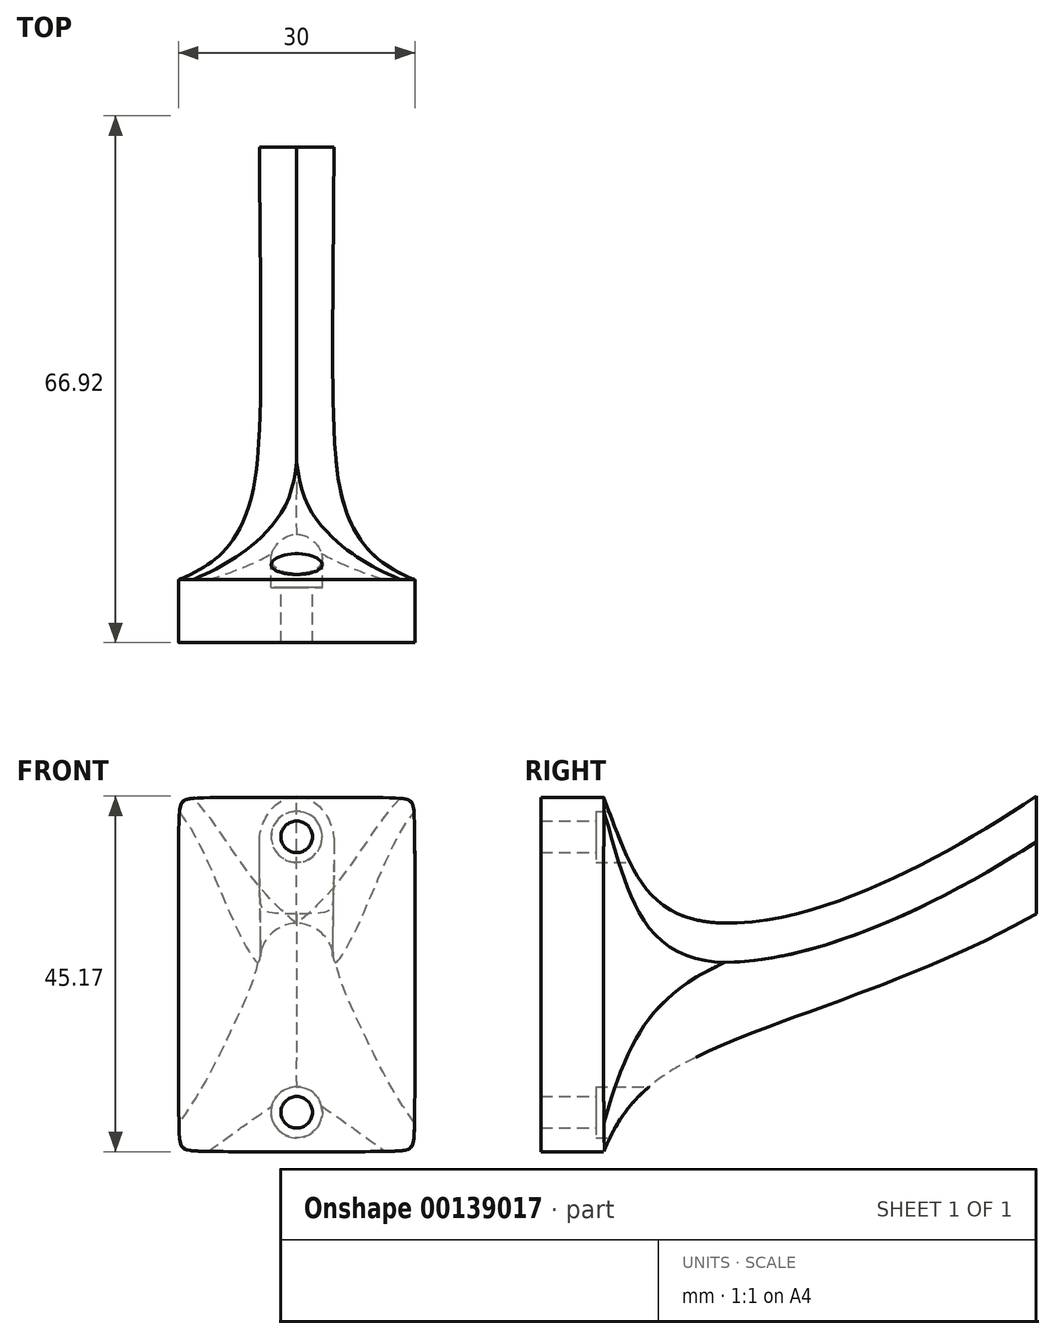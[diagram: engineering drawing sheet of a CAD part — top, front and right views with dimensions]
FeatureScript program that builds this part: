
annotation { "Feature Type Name" : "Feature", "Feature Type Description" : "" }
export const myFeature = defineFeature(function(context is Context, id is Id, definition is map)
    precondition{}
    {
        {
            var Q0;
            Q0=qCreatedBy(makeId("Right.planeOp"),FACE);
            var sketch = newSketch(context, id + "F0", { "sketchPlane" : qUnion([Q0])});
            skLineSegment(sketch, "E0", {"start": v(0, 0) * mm, "end": v(0, 45) * mm});
            skLineSegment(sketch, "E1", {"start": v(54.94, 45.17) * mm, "end": v(54.94, 30.17) * mm});
            skFitSpline(sketch, "E2", {"points": [v(0, 45) * mm, v(8.8, 30.52) * mm, v(54.94, 45.17) * mm], "startDerivative": vector(18.6, -48.26) * mm, "endDerivative": vector(97.53, 66.1) * mm});
            skFitSpline(sketch, "E3", {"points": [v(0, 0) * mm, v(8.62, 10.3) * mm, v(54.94, 30.17) * mm], "startDerivative": vector(13.75, 34.06) * mm, "endDerivative": vector(78.66, 44.42) * mm});
            skSolve(sketch);
        }
        {
            var Q0;
            Q0 = qSketchRegion(id + "F0", true);
            extrude(context, id + "F1", {"entities" : qUnion([Q0]), "endBound" : BoundingType.SYMMETRIC, "depth" : 30 * mm});
        }
        {
            var Q0;
            Q0=makeQuery(id+"F1.opExtrude","SWEPT_FACE",FACE,{"disambiguationData":[OSD([sQuery(id+"F0.wireOp",EDGE,"E0")])]});
            extrude(context, id + "F2", {"entities" : qUnion([Q0]), "operationType" : NewBodyOperationType.ADD, "depth" : 8 * mm});
        }
        {
            var Q0;
            Q0=qCreatedBy(makeId("Top.planeOp"),FACE);
            var sketch = newSketch(context, id + "F3", { "sketchPlane" : qUnion([Q0])});
            skLineSegment(sketch, "E4", {"start": v(-28.38, 62.27) * mm, "end": v(-28.38, 0) * mm});
            skLineSegment(sketch, "E5", {"start": v(-28.38, 0) * mm, "end": v(-15, 0) * mm});
            skLineSegment(sketch, "E6", {"start": v(-28.38, 62.27) * mm, "end": v(-13.4, 62.27) * mm});
            skFitSpline(sketch, "E7", {"points": [v(-15, 0) * mm, v(-6.95, 7.07) * mm, v(-4.77, 59.21) * mm], "startDerivative": vector(43.42, 16.68) * mm, "endDerivative": vector(-0.83, 161.44) * mm});
            skLineSegment(sketch, "E8", {"start": v(-13.4, 62.27) * mm, "end": v(-4.77, 59.21) * mm});
            skLineSegment(sketch, "E9.MirrorCS", {"start": v(13.4, 62.27) * mm, "end": v(4.77, 59.21) * mm});
            skFitSpline(sketch, "E10.MirrorCS", {"points": [v(15, 0) * mm, v(6.95, 7.07) * mm, v(4.77, 59.21) * mm], "startDerivative": vector(-43.42, 16.68) * mm, "endDerivative": vector(0.83, 161.44) * mm});
            skLineSegment(sketch, "E11.MirrorCS", {"start": v(28.38, 62.27) * mm, "end": v(13.4, 62.27) * mm});
            skLineSegment(sketch, "E12.MirrorCS", {"start": v(28.38, 62.27) * mm, "end": v(28.38, 0) * mm});
            skLineSegment(sketch, "E13.MirrorCS", {"start": v(28.38, 0) * mm, "end": v(15, 0) * mm});
            skSolve(sketch);
        }
        {
            var Q0;
            Q0 = qSketchRegion(id + "F3", true);
            extrude(context, id + "F4", {"entities" : qUnion([Q0]), "operationType" : NewBodyOperationType.REMOVE, "endBound" : BoundingType.THROUGH_ALL, "depth" : 25 * mm});
        }
        {
            var Q0;
            Q0=qCreatedBy(makeId("Front.planeOp"),FACE);
            cPlane(context, id + "F5", {"entities" : qUnion([Q0]), "cplaneType" : CPlaneType.OFFSET, "offset" : 7 * mm, "oppositeDirection" : true, "width" : 150 * mm, "height" : 150 * mm});
        }
        {
            var Q0;
            Q0=qCreatedBy(id+"F5.planeOp",FACE);
            var sketch = newSketch(context, id + "F6", { "sketchPlane" : qUnion([Q0])});
            skPoint(sketch, "E14", {"position": v(0, 5) * mm});
            skPoint(sketch, "E15", {"position": v(0, 40) * mm});
            skSolve(sketch);
        }
        {
            var Q0;
            Q0=sQuery(id+"F6.wireOp",VERTEX,"E15");
            var Q1;
            Q1=sQuery(id+"F6.wireOp",VERTEX,"E14");
            var Q2;
            Q2=makeQuery(id+"F1.opExtrude","SWEPT_BODY",BODY,{"disambiguationData":[OSD([sQuery(id+"F0.wireOp",EDGE,"E0"),sQuery(id+"F0.wireOp",EDGE,"E1"),sQuery(id+"F0.wireOp",EDGE,"E2"),sQuery(id+"F0.wireOp",EDGE,"E3")])]});
            hole(context, id + "F7", {"style" : HoleStyle.C_BORE, "endStyle" : HoleEndStyle.THROUGH, "oppositeDirection" : true, "standardTappedOrClearance" : lookupTablePath({ "standard" : "ISO", "size" : "4", "type" : "Drilled" }), "standardBlindInLast" : lookupTablePath({ "standard" : "ISO", "size" : "4", "type" : "Drilled" }), "holeDiameter" : 4 * mm, "cBoreDiameter" : 6.5 * mm, "cBoreDepth" : 8 * mm, "startFromSketch" : true, "locations" : qUnion([Q0, Q1]), "scope" : qUnion([Q2]), "isTappedThrough" : true});
        }
        {
            var Q0;
            Q0=makeQuery(id+"F4.boolean.opBoolean","INTERSECT",EDGE,{"derivedFrom":[makeQuery(id+"F1.opExtrude","SWEPT_FACE",FACE,{"disambiguationData":[OSD([sQuery(id+"F0.wireOp",EDGE,"E2")])]}),makeQuery(id+"F4.opExtrude","SWEPT_FACE",FACE,{"disambiguationData":[OSD([sQuery(id+"F3.wireOp",EDGE,"E10.MirrorCS")])]})]});
            var Q1;
            Q1=makeQuery(id+"F4.boolean.opBoolean","INTERSECT",EDGE,{"derivedFrom":[makeQuery(id+"F1.opExtrude","SWEPT_FACE",FACE,{"disambiguationData":[OSD([sQuery(id+"F0.wireOp",EDGE,"E2")])]}),makeQuery(id+"F4.opExtrude","SWEPT_FACE",FACE,{"disambiguationData":[OSD([sQuery(id+"F3.wireOp",EDGE,"E7")])]})]});
            fillet(context, id + "F8", {"entities" : qUnion([Q0, Q1]), "radius" : 5 * mm, "tangentPropagation" : true, "allowEdgeOverflow" : false});
        }
        {
            var Q0;
            {var subQ0=sQuery(id+"F0.wireOp",EDGE,"E2");var subQ1=sQuery(id+"F0.wireOp",EDGE,"E0");Q0=makeQuery(id+"F2.opExtrude","SWEPT_EDGE",EDGE,{"disambiguationData":[OSD([subQ1,subQ0]),TDD([makeQuery(id+"F1.opExtrude","CAP_VERTEX",VERTEX,{"disambiguationData":[OSD([subQ1,subQ0])],"isStart":false})])]});}
            var Q1;
            {var subQ0=sQuery(id+"F0.wireOp",EDGE,"E2");var subQ1=sQuery(id+"F0.wireOp",EDGE,"E0");Q1=makeQuery(id+"F2.opExtrude","SWEPT_EDGE",EDGE,{"disambiguationData":[OSD([subQ1,subQ0]),TDD([makeQuery(id+"F1.opExtrude","CAP_VERTEX",VERTEX,{"disambiguationData":[OSD([subQ1,subQ0])],"isStart":true})])]});}
            var Q2;
            {var subQ0=sQuery(id+"F0.wireOp",EDGE,"E3");var subQ1=sQuery(id+"F0.wireOp",EDGE,"E0");Q2=makeQuery(id+"F2.opExtrude","SWEPT_EDGE",EDGE,{"disambiguationData":[OSD([subQ1,subQ0]),TDD([makeQuery(id+"F1.opExtrude","CAP_VERTEX",VERTEX,{"disambiguationData":[OSD([subQ1,subQ0])],"isStart":true})])]});}
            var Q3;
            {var subQ0=sQuery(id+"F0.wireOp",EDGE,"E3");var subQ1=sQuery(id+"F0.wireOp",EDGE,"E0");Q3=makeQuery(id+"F2.opExtrude","SWEPT_EDGE",EDGE,{"disambiguationData":[OSD([subQ1,subQ0]),TDD([makeQuery(id+"F1.opExtrude","CAP_VERTEX",VERTEX,{"disambiguationData":[OSD([subQ1,subQ0])],"isStart":false})])]});}
            var Q4;
            Q4=makeQuery(id+"F4.boolean.opBoolean","INTERSECT",EDGE,{"derivedFrom":[makeQuery(id+"F1.opExtrude","SWEPT_FACE",FACE,{"disambiguationData":[OSD([sQuery(id+"F0.wireOp",EDGE,"E3")])]}),makeQuery(id+"F4.opExtrude","SWEPT_FACE",FACE,{"disambiguationData":[OSD([sQuery(id+"F3.wireOp",EDGE,"E10.MirrorCS")])]})]});
            var Q5;
            Q5=makeQuery(id+"F4.boolean.opBoolean","INTERSECT",EDGE,{"derivedFrom":[makeQuery(id+"F1.opExtrude","SWEPT_FACE",FACE,{"disambiguationData":[OSD([sQuery(id+"F0.wireOp",EDGE,"E3")])]}),makeQuery(id+"F4.opExtrude","SWEPT_FACE",FACE,{"disambiguationData":[OSD([sQuery(id+"F3.wireOp",EDGE,"E7")])]})]});
            fillet(context, id + "F9", {"entities" : qUnion([Q0, Q1, Q2, Q3, Q4, Q5]), "radius" : 10 * mm, "rho" : 0.9, "crossSection" : FilletCrossSection.CONIC, "allowEdgeOverflow" : false});
        }
    });
